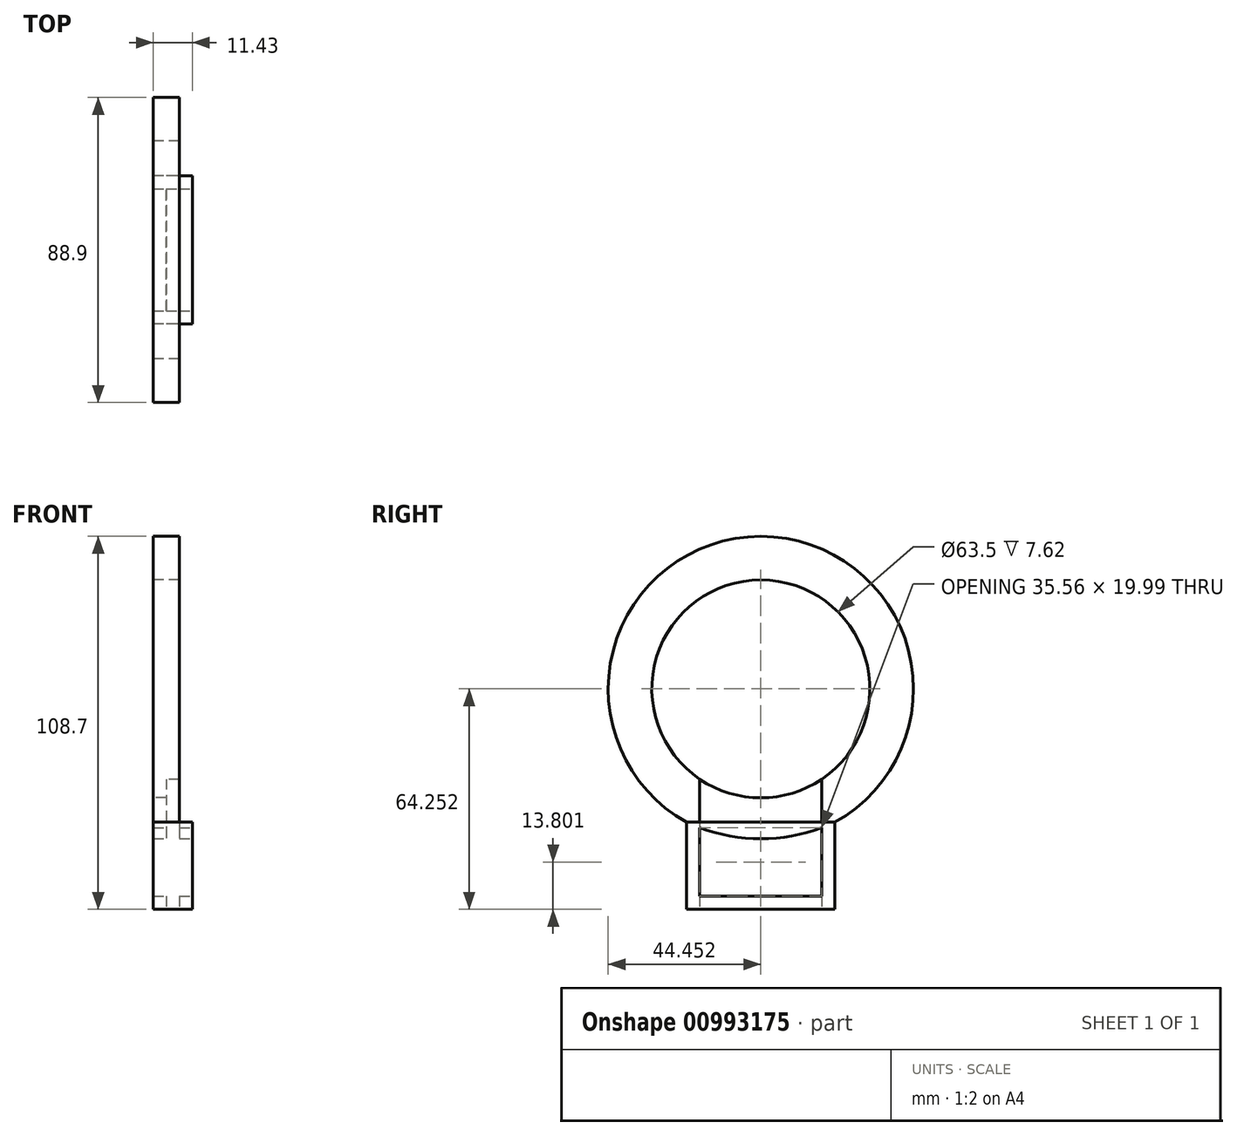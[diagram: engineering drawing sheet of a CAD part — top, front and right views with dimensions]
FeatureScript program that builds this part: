
annotation { "Feature Type Name" : "Feature", "Feature Type Description" : "" }
export const myFeature = defineFeature(function(context is Context, id is Id, definition is map)
    precondition{}
    {
        {
            var Q0;
            Q0=qCreatedBy(makeId("Right.planeOp"),FACE);
            var sketch = newSketch(context, id + "F0", { "sketchPlane" : qUnion([Q0])});
            skCircle(sketch, "E0", {"center": v(-42.83, -236.19) * mm, "radius": 44.45 * mm});
            skCircle(sketch, "E1", {"center": v(-42.83, -236.19) * mm, "radius": 31.75 * mm});
            skLineSegment(sketch, "E2.bottom", {"start": v(-21.24, -275.04) * mm, "end": v(-64.42, -275.04) * mm});
            skLineSegment(sketch, "E2.top", {"start": v(-21.24, -300.44) * mm, "end": v(-64.42, -300.44) * mm});
            skLineSegment(sketch, "E2.left", {"start": v(-21.24, -275.04) * mm, "end": v(-21.24, -300.44) * mm});
            skLineSegment(sketch, "E2.right", {"start": v(-64.42, -275.04) * mm, "end": v(-64.42, -300.44) * mm});
            skPoint(sketch, "E2.middle", {"position": v(-42.83, -287.74) * mm});
            skSolve(sketch);
        }
        {
            var Q0;
            {var subQ0=sQuery(id+"F0.wireOp",EDGE,"E2.bottom");Q0=makeQuery(id+"F0.imprint","IMPRINT",FACE,{"disambiguationData":[TD([[makeQuery(id+"F0.imprint","IMPRINT",EDGE,{"derivedFrom":subQ0}),1.0]])]});}
            var Q1;
            Q1=makeQuery(id+"F0.imprint","IMPRINT",FACE,{"disambiguationData":[TD([[makeQuery(id+"F0.imprint","IMPRINT",EDGE,{"derivedFrom":sQuery(id+"F0.wireOp",EDGE,"E2.top")}),-1.0]])]});
            extrude(context, id + "F1", {"entities" : qUnion([Q0, Q1]), "depth" : 11.43 * mm, "offsetDistance" : 25.4 * mm});
        }
        {
            var Q0;
            Q0=makeQuery(id+"F1.opExtrude","SWEPT_FACE",FACE,{"disambiguationData":[OSD([sQuery(id+"F0.wireOp",EDGE,"E2.top")])]});
            var sketch = newSketch(context, id + "F2", { "sketchPlane" : qUnion([Q0])});
            skLineSegment(sketch, "E3.bottom", {"start": v(3.8, 60.6) * mm, "end": v(7.62, 60.6) * mm});
            skLineSegment(sketch, "E3.top", {"start": v(3.81, 25.05) * mm, "end": v(7.62, 25.05) * mm});
            skLineSegment(sketch, "E3.left", {"start": v(3.8, 60.6) * mm, "end": v(3.81, 25.05) * mm});
            skLineSegment(sketch, "E3.right", {"start": v(7.62, 60.6) * mm, "end": v(7.62, 25.05) * mm});
            skSolve(sketch);
        }
        {
            var Q0;
            Q0=makeQuery(id+"F1.opExtrude","CAP_FACE",FACE,{"disambiguationData":[OSD([sQuery(id+"F0.wireOp",EDGE,"E0"),sQuery(id+"F0.wireOp",EDGE,"E1"),sQuery(id+"F0.wireOp",EDGE,"E2.top"),sQuery(id+"F0.wireOp",EDGE,"E2.left"),sQuery(id+"F0.wireOp",EDGE,"E2.right")])],"isStart":false});
            var sketch = newSketch(context, id + "F3", { "sketchPlane" : qUnion([Q0])});
            skLineSegment(sketch, "E4.bottom", {"start": v(-60.6, -296.63) * mm, "end": v(-25.05, -296.63) * mm});
            skLineSegment(sketch, "E4.top", {"start": v(-60.6, -275.04) * mm, "end": v(-25.05, -275.04) * mm});
            skLineSegment(sketch, "E4.left", {"start": v(-60.6, -296.63) * mm, "end": v(-60.6, -275.04) * mm});
            skLineSegment(sketch, "E4.right", {"start": v(-25.05, -296.63) * mm, "end": v(-25.05, -275.04) * mm});
            skArc(sketch, "E5", {"start": v(-64.42, -275.04) * mm, "mid": v(-42.83, -279.86) * mm, "end": v(-21.24, -275.04) * mm});
            skSolve(sketch);
        }
        {
            var Q0;
            Q0=makeQuery(id+"F0.imprint","IMPRINT",FACE,{"disambiguationData":[TD([[makeQuery(id+"F0.imprint","IMPRINT",EDGE,{"derivedFrom":sQuery(id+"F0.wireOp",EDGE,"E1")}),-1.0]])]});
            extrude(context, id + "F4", {"entities" : qUnion([Q0]), "operationType" : NewBodyOperationType.ADD, "depth" : 7.62 * mm, "offsetDistance" : 25.4 * mm});
        }
        {
            var Q0;
            Q0=makeQuery(id+"F2.imprint","IMPRINT",FACE,{"disambiguationData":[TD([[makeQuery(id+"F2.imprint","IMPRINT",EDGE,{"derivedFrom":sQuery(id+"F2.wireOp",EDGE,"E3.bottom")}),-1.0]])]});
            extrude(context, id + "F5", {"entities" : qUnion([Q0]), "operationType" : NewBodyOperationType.REMOVE, "oppositeDirection" : true, "depth" : 76.2 * mm, "offsetDistance" : 25.4 * mm});
        }
        {
            var Q0;
            {var subQ0=sQuery(id+"F3.wireOp",EDGE,"E4.bottom");Q0=makeQuery(id+"F3.imprint","IMPRINT",FACE,{"disambiguationData":[TD([[makeQuery(id+"F3.imprint","IMPRINT",EDGE,{"derivedFrom":subQ0}),1.0]])]});}
            extrude(context, id + "F6", {"entities" : qUnion([Q0]), "operationType" : NewBodyOperationType.REMOVE, "oppositeDirection" : true, "depth" : 76.2 * mm, "offsetDistance" : 25.4 * mm});
        }
    });
